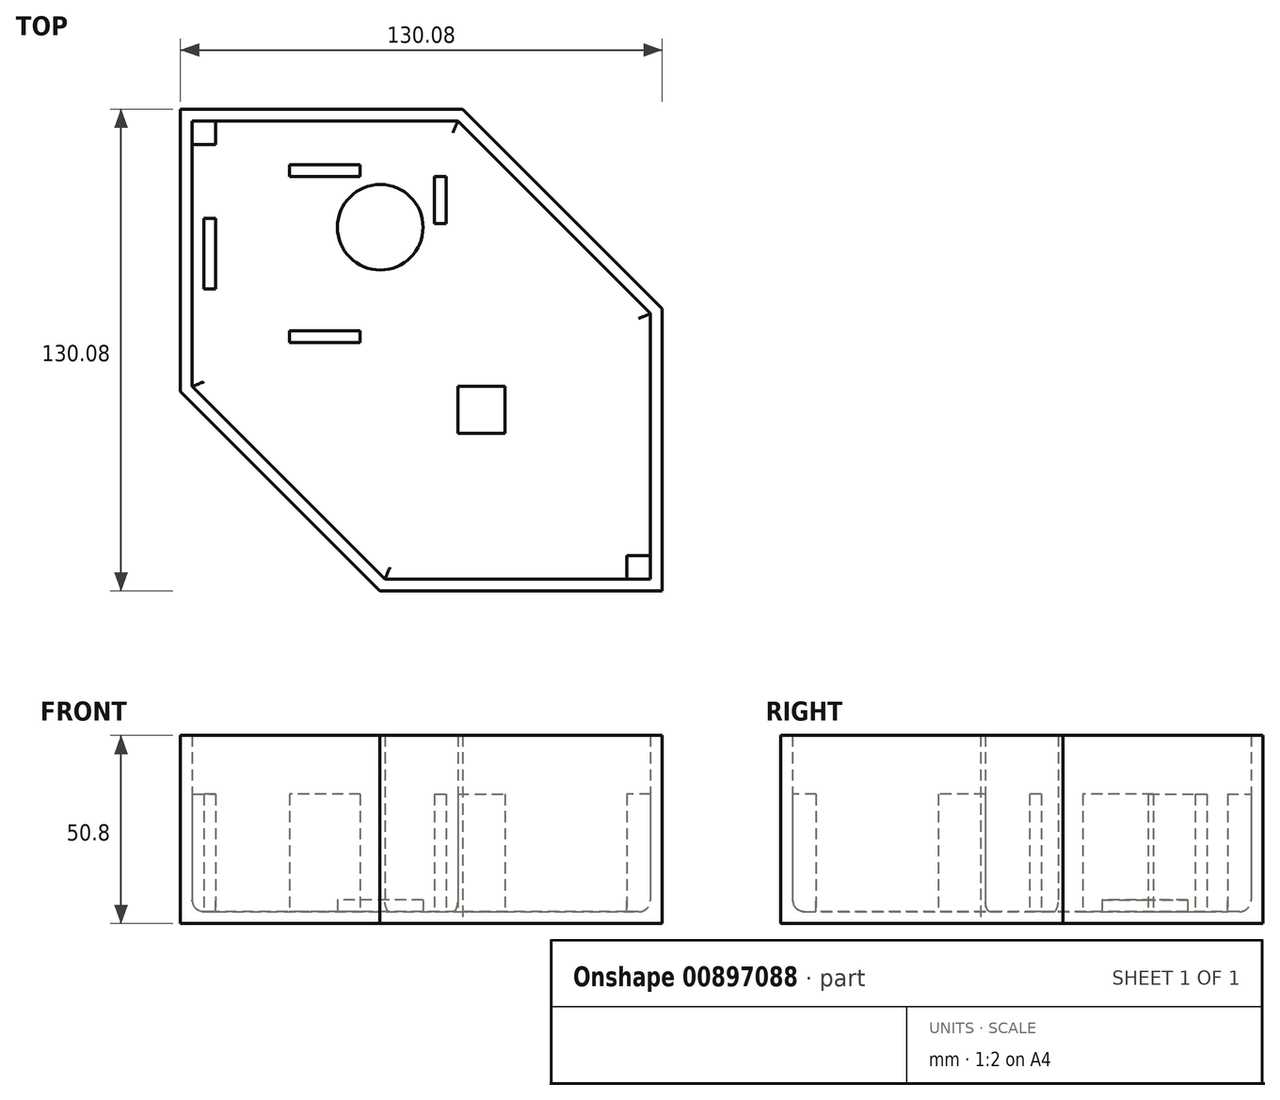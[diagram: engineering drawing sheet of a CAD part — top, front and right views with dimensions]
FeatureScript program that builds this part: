
annotation { "Feature Type Name" : "Feature", "Feature Type Description" : "" }
export const myFeature = defineFeature(function(context is Context, id is Id, definition is map)
    precondition{}
    {
        {
            var Q0;
            Q0=qCreatedBy(makeId("Top.planeOp"),FACE);
            var sketch = newSketch(context, id + "F0", { "sketchPlane" : qUnion([Q0])});
            skLineSegment(sketch, "E0", {"start": v(0, 0) * mm, "end": v(-53.88, 53.88) * mm});
            skLineSegment(sketch, "E1", {"start": v(-53.88, 53.88) * mm, "end": v(-53.88, 130.08) * mm});
            skLineSegment(sketch, "E2", {"start": v(-53.88, 130.08) * mm, "end": v(22.32, 130.08) * mm});
            skLineSegment(sketch, "E3", {"start": v(22.32, 130.08) * mm, "end": v(76.2, 76.2) * mm});
            skLineSegment(sketch, "E4", {"start": v(76.2, 76.2) * mm, "end": v(76.2, 0) * mm});
            skLineSegment(sketch, "E5", {"start": v(76.2, 0) * mm, "end": v(0, 0) * mm});
            skSolve(sketch);
        }
        {
            var Q0;
            Q0=makeQuery(id+"F0.imprint","IMPRINT",FACE,{"disambiguationData":[TD([[makeQuery(id+"F0.imprint","IMPRINT",EDGE,{"derivedFrom":sQuery(id+"F0.wireOp",EDGE,"E0")}),-1.0]])]});
            extrude(context, id + "F1", {"entities" : qUnion([Q0]), "depth" : 50.8 * mm, "offsetDistance" : 25.4 * mm});
        }
        {
            var Q0;
            Q0=makeQuery(id+"F1.opExtrude","CAP_FACE",FACE,{"disambiguationData":[OSD([sQuery(id+"F0.wireOp",EDGE,"E0"),sQuery(id+"F0.wireOp",EDGE,"E1"),sQuery(id+"F0.wireOp",EDGE,"E2"),sQuery(id+"F0.wireOp",EDGE,"E3"),sQuery(id+"F0.wireOp",EDGE,"E4"),sQuery(id+"F0.wireOp",EDGE,"E5")])],"isStart":false});
            shell(context, id + "F2", {"entities" : qUnion([Q0]), "thickness" : 3.17 * mm});
        }
        {
            var Q0;
            Q0=makeQuery(id+"F2.opShell","OFFSET_FACE",FACE,{"disambiguationData":[OSD([sQuery(id+"F0.wireOp",EDGE,"E0"),sQuery(id+"F0.wireOp",EDGE,"E1"),sQuery(id+"F0.wireOp",EDGE,"E2"),sQuery(id+"F0.wireOp",EDGE,"E3"),sQuery(id+"F0.wireOp",EDGE,"E4"),sQuery(id+"F0.wireOp",EDGE,"E5")])]});
            var sketch = newSketch(context, id + "F3", { "sketchPlane" : qUnion([Q0])});
            skLineSegment(sketch, "E6", {"start": v(21, 126.9) * mm, "end": v(21, 3.17) * mm, "construction": true});
            skLineSegment(sketch, "E7", {"start": v(-50.7, 55.2) * mm, "end": v(73.03, 55.2) * mm, "construction": true});
            skLineSegment(sketch, "E8", {"start": v(-14.85, 126.9) * mm, "end": v(-14.85, 55.2) * mm, "construction": true});
            skLineSegment(sketch, "E9", {"start": v(-50.7, 91.05) * mm, "end": v(21, 91.05) * mm, "construction": true});
            skLineSegment(sketch, "E10.bottom", {"start": v(14.69, 111.84) * mm, "end": v(-44.4, 111.84) * mm, "construction": true});
            skLineSegment(sketch, "E10.top", {"start": v(14.69, 70.26) * mm, "end": v(-44.4, 70.26) * mm, "construction": true});
            skLineSegment(sketch, "E10.left", {"start": v(14.69, 111.84) * mm, "end": v(14.69, 70.26) * mm, "construction": true});
            skLineSegment(sketch, "E10.right", {"start": v(-44.4, 111.84) * mm, "end": v(-44.4, 70.26) * mm, "construction": true});
            skPoint(sketch, "E10.middle", {"position": v(-14.85, 91.05) * mm});
            skLineSegment(sketch, "E11.bottom", {"start": v(-5.33, 111.84) * mm, "end": v(-24.38, 111.84) * mm});
            skLineSegment(sketch, "E11.top", {"start": v(-5.33, 115.02) * mm, "end": v(-24.38, 115.02) * mm});
            skLineSegment(sketch, "E11.left", {"start": v(-5.33, 111.84) * mm, "end": v(-5.33, 115.02) * mm});
            skLineSegment(sketch, "E11.right", {"start": v(-24.38, 111.84) * mm, "end": v(-24.38, 115.02) * mm});
            skPoint(sketch, "E11.middle", {"position": v(-14.85, 113.43) * mm});
            skLineSegment(sketch, "E12.bottom", {"start": v(-5.33, 70.26) * mm, "end": v(-24.38, 70.26) * mm});
            skLineSegment(sketch, "E12.top", {"start": v(-5.33, 67.09) * mm, "end": v(-24.38, 67.09) * mm});
            skLineSegment(sketch, "E12.left", {"start": v(-5.33, 70.26) * mm, "end": v(-5.33, 67.09) * mm});
            skLineSegment(sketch, "E12.right", {"start": v(-24.38, 70.26) * mm, "end": v(-24.38, 67.09) * mm});
            skPoint(sketch, "E12.middle", {"position": v(-14.85, 68.67) * mm});
            skLineSegment(sketch, "E13.bottom", {"start": v(-44.4, 100.58) * mm, "end": v(-47.57, 100.58) * mm});
            skLineSegment(sketch, "E13.top", {"start": v(-44.4, 81.53) * mm, "end": v(-47.57, 81.53) * mm});
            skLineSegment(sketch, "E13.left", {"start": v(-44.4, 100.58) * mm, "end": v(-44.4, 81.53) * mm});
            skLineSegment(sketch, "E13.right", {"start": v(-47.57, 100.58) * mm, "end": v(-47.57, 81.53) * mm});
            skPoint(sketch, "E13.middle", {"position": v(-45.98, 91.05) * mm});
            skLineSegment(sketch, "E14.bottom", {"start": v(14.69, 99.14) * mm, "end": v(17.86, 99.14) * mm});
            skLineSegment(sketch, "E14.top", {"start": v(14.69, 111.84) * mm, "end": v(17.86, 111.84) * mm});
            skLineSegment(sketch, "E14.left", {"start": v(14.69, 99.14) * mm, "end": v(14.69, 111.84) * mm});
            skLineSegment(sketch, "E14.right", {"start": v(17.86, 99.14) * mm, "end": v(17.86, 111.84) * mm});
            skLineSegment(sketch, "E15", {"start": v(-24.7, 29.19) * mm, "end": v(47.01, 100.9) * mm, "construction": true});
            skLineSegment(sketch, "E16.bottom", {"start": v(21, 55.2) * mm, "end": v(33.7, 55.2) * mm});
            skLineSegment(sketch, "E16.top", {"start": v(21, 42.5) * mm, "end": v(33.7, 42.5) * mm});
            skLineSegment(sketch, "E16.left", {"start": v(21, 55.2) * mm, "end": v(21, 42.5) * mm});
            skLineSegment(sketch, "E16.right", {"start": v(33.7, 55.2) * mm, "end": v(33.7, 42.5) * mm});
            skLineSegment(sketch, "E17.bottom", {"start": v(73.02, 3.17) * mm, "end": v(66.68, 3.17) * mm});
            skLineSegment(sketch, "E17.top", {"start": v(73.03, 9.53) * mm, "end": v(66.68, 9.53) * mm});
            skLineSegment(sketch, "E17.left", {"start": v(73.02, 3.17) * mm, "end": v(73.02, 9.53) * mm});
            skLineSegment(sketch, "E17.right", {"start": v(66.68, 3.17) * mm, "end": v(66.68, 9.53) * mm});
            skLineSegment(sketch, "E18.bottom", {"start": v(-50.7, 126.9) * mm, "end": v(-44.36, 126.9) * mm});
            skLineSegment(sketch, "E18.top", {"start": v(-50.7, 120.56) * mm, "end": v(-44.36, 120.56) * mm});
            skLineSegment(sketch, "E18.left", {"start": v(-50.7, 126.9) * mm, "end": v(-50.7, 120.56) * mm});
            skLineSegment(sketch, "E18.right", {"start": v(-44.36, 126.9) * mm, "end": v(-44.36, 120.56) * mm});
            skCircle(sketch, "E19", {"center": v(0.06, 98.2) * mm, "radius": 11.56 * mm, "construction": true});
            skSolve(sketch);
        }
        {
            var Q0;
            Q0 = qSketchRegion(id + "F3", true);
            extrude(context, id + "F4", {"entities" : qUnion([Q0]), "operationType" : NewBodyOperationType.ADD, "depth" : 31.75 * mm, "offsetDistance" : 25.4 * mm});
        }
        {
            var Q0;
            Q0=makeQuery(id+"F2.opShell","OFFSET_FACE",FACE,{"disambiguationData":[OSD([sQuery(id+"F0.wireOp",EDGE,"E0"),sQuery(id+"F0.wireOp",EDGE,"E1"),sQuery(id+"F0.wireOp",EDGE,"E2"),sQuery(id+"F0.wireOp",EDGE,"E3"),sQuery(id+"F0.wireOp",EDGE,"E4"),sQuery(id+"F0.wireOp",EDGE,"E5")])]});
            var sketch = newSketch(context, id + "F5", { "sketchPlane" : qUnion([Q0])});
            skCircle(sketch, "E20", {"center": v(0.06, 98.2) * mm, "radius": 11.56 * mm});
            skSolve(sketch);
        }
        {
            var Q0;
            Q0 = qSketchRegion(id + "F5", true);
            extrude(context, id + "F6", {"entities" : qUnion([Q0]), "operationType" : NewBodyOperationType.ADD, "depth" : 3.17 * mm, "offsetDistance" : 25.4 * mm});
        }
        {
            var Q0;
            Q0=makeQuery(id+"F4.opExtrude","CAP_EDGE",EDGE,{"disambiguationData":[OSD([sQuery(id+"F3.wireOp",EDGE,"E14.right")])],"isStart":true});
            var Q1;
            Q1=makeQuery(id+"F4.opExtrude","CAP_EDGE",EDGE,{"disambiguationData":[OSD([sQuery(id+"F3.wireOp",EDGE,"E14.top")])],"isStart":true});
            var Q2;
            Q2=makeQuery(id+"F4.opExtrude","CAP_EDGE",EDGE,{"disambiguationData":[OSD([sQuery(id+"F3.wireOp",EDGE,"E14.bottom")])],"isStart":true});
            var Q3;
            Q3=makeQuery(id+"F4.opExtrude","CAP_EDGE",EDGE,{"disambiguationData":[OSD([sQuery(id+"F3.wireOp",EDGE,"E12.top")])],"isStart":true});
            var Q4;
            Q4=makeQuery(id+"F4.opExtrude","CAP_EDGE",EDGE,{"disambiguationData":[OSD([sQuery(id+"F3.wireOp",EDGE,"E12.left")])],"isStart":true});
            var Q5;
            Q5=makeQuery(id+"F4.opExtrude","CAP_EDGE",EDGE,{"disambiguationData":[OSD([sQuery(id+"F3.wireOp",EDGE,"E12.right")])],"isStart":true});
            var Q6;
            Q6=makeQuery(id+"F4.opExtrude","CAP_EDGE",EDGE,{"disambiguationData":[OSD([sQuery(id+"F3.wireOp",EDGE,"E13.top")])],"isStart":true});
            var Q7;
            Q7=makeQuery(id+"F4.opExtrude","CAP_EDGE",EDGE,{"disambiguationData":[OSD([sQuery(id+"F3.wireOp",EDGE,"E13.right")])],"isStart":true});
            var Q8;
            Q8=makeQuery(id+"F4.opExtrude","CAP_EDGE",EDGE,{"disambiguationData":[OSD([sQuery(id+"F3.wireOp",EDGE,"E13.bottom")])],"isStart":true});
            var Q9;
            Q9=makeQuery(id+"F4.opExtrude","CAP_EDGE",EDGE,{"disambiguationData":[OSD([sQuery(id+"F3.wireOp",EDGE,"E11.right")])],"isStart":true});
            var Q10;
            Q10=makeQuery(id+"F4.opExtrude","CAP_EDGE",EDGE,{"disambiguationData":[OSD([sQuery(id+"F3.wireOp",EDGE,"E11.top")])],"isStart":true});
            var Q11;
            Q11=makeQuery(id+"F4.opExtrude","CAP_EDGE",EDGE,{"disambiguationData":[OSD([sQuery(id+"F3.wireOp",EDGE,"E11.left")])],"isStart":true});
            var Q12;
            Q12=makeQuery(id+"F4.opExtrude","CAP_EDGE",EDGE,{"disambiguationData":[OSD([sQuery(id+"F3.wireOp",EDGE,"E16.bottom")])],"isStart":true});
            var Q13;
            Q13=makeQuery(id+"F4.opExtrude","CAP_EDGE",EDGE,{"disambiguationData":[OSD([sQuery(id+"F3.wireOp",EDGE,"E16.right")])],"isStart":true});
            var Q14;
            Q14=makeQuery(id+"F4.opExtrude","CAP_EDGE",EDGE,{"disambiguationData":[OSD([sQuery(id+"F3.wireOp",EDGE,"E16.top")])],"isStart":true});
            var Q15;
            Q15=makeQuery(id+"F4.opExtrude","CAP_EDGE",EDGE,{"disambiguationData":[OSD([sQuery(id+"F3.wireOp",EDGE,"E16.left")])],"isStart":true});
            var Q16;
            Q16=makeQuery(id+"F4.opExtrude","CAP_EDGE",EDGE,{"disambiguationData":[OSD([sQuery(id+"F3.wireOp",EDGE,"E18.top")])],"isStart":true});
            var Q17;
            Q17=makeQuery(id+"F4.opExtrude","CAP_EDGE",EDGE,{"disambiguationData":[OSD([sQuery(id+"F3.wireOp",EDGE,"E18.right")])],"isStart":true});
            var Q18;
            Q18=makeQuery(id+"F4.opExtrude","CAP_EDGE",EDGE,{"disambiguationData":[OSD([sQuery(id+"F3.wireOp",EDGE,"E17.top")])],"isStart":true});
            var Q19;
            Q19=makeQuery(id+"F4.opExtrude","CAP_EDGE",EDGE,{"disambiguationData":[OSD([sQuery(id+"F3.wireOp",EDGE,"E17.right")])],"isStart":true});
            var Q20;
            {var subQ0=sQuery(id+"F0.wireOp",EDGE,"E2");Q20=makeQuery(id+"F2.opShell","OFFSET_EDGE",EDGE,{"disambiguationData":[OSD([subQ0]),TDD([makeQuery(id+"F1.opExtrude","CAP_EDGE",EDGE,{"disambiguationData":[OSD([subQ0])],"isStart":true})])]});}
            var Q21;
            {var subQ0=sQuery(id+"F0.wireOp",EDGE,"E3");Q21=makeQuery(id+"F2.opShell","OFFSET_EDGE",EDGE,{"disambiguationData":[OSD([subQ0]),TDD([makeQuery(id+"F1.opExtrude","CAP_EDGE",EDGE,{"disambiguationData":[OSD([subQ0])],"isStart":true})])]});}
            var Q22;
            {var subQ0=sQuery(id+"F0.wireOp",EDGE,"E4");Q22=makeQuery(id+"F2.opShell","OFFSET_EDGE",EDGE,{"disambiguationData":[OSD([subQ0]),TDD([makeQuery(id+"F1.opExtrude","CAP_EDGE",EDGE,{"disambiguationData":[OSD([subQ0])],"isStart":true})])]});}
            var Q23;
            {var subQ0=sQuery(id+"F0.wireOp",EDGE,"E5");Q23=makeQuery(id+"F2.opShell","OFFSET_EDGE",EDGE,{"disambiguationData":[OSD([subQ0]),TDD([makeQuery(id+"F1.opExtrude","CAP_EDGE",EDGE,{"disambiguationData":[OSD([subQ0])],"isStart":true})])]});}
            var Q24;
            {var subQ0=sQuery(id+"F0.wireOp",EDGE,"E0");Q24=makeQuery(id+"F2.opShell","OFFSET_EDGE",EDGE,{"disambiguationData":[OSD([subQ0]),TDD([makeQuery(id+"F1.opExtrude","CAP_EDGE",EDGE,{"disambiguationData":[OSD([subQ0])],"isStart":true})])]});}
            var Q25;
            {var subQ0=sQuery(id+"F0.wireOp",EDGE,"E1");Q25=makeQuery(id+"F2.opShell","OFFSET_EDGE",EDGE,{"disambiguationData":[OSD([subQ0]),TDD([makeQuery(id+"F1.opExtrude","CAP_EDGE",EDGE,{"disambiguationData":[OSD([subQ0])],"isStart":true})])]});}
            var Q26;
            Q26=makeQuery(id+"F4.opExtrude","SWEPT_EDGE",EDGE,{"disambiguationData":[OSD([sQuery(id+"F0.wireOp",EDGE,"E1"),sQuery(id+"F3.wireOp",EDGE,"E18.top"),sQuery(id+"F3.wireOp",EDGE,"E18.left")])]});
            var Q27;
            Q27=makeQuery(id+"F4.opExtrude","SWEPT_EDGE",EDGE,{"disambiguationData":[OSD([sQuery(id+"F0.wireOp",EDGE,"E2"),sQuery(id+"F3.wireOp",EDGE,"E18.bottom"),sQuery(id+"F3.wireOp",EDGE,"E18.right")])]});
            var Q28;
            Q28=makeQuery(id+"F4.opExtrude","SWEPT_EDGE",EDGE,{"disambiguationData":[OSD([sQuery(id+"F0.wireOp",EDGE,"E4"),sQuery(id+"F3.wireOp",EDGE,"E17.top"),sQuery(id+"F3.wireOp",EDGE,"E17.left")])]});
            var Q29;
            Q29=makeQuery(id+"F4.opExtrude","SWEPT_EDGE",EDGE,{"disambiguationData":[OSD([sQuery(id+"F0.wireOp",EDGE,"E5"),sQuery(id+"F3.wireOp",EDGE,"E17.bottom"),sQuery(id+"F3.wireOp",EDGE,"E17.right")])]});
            fillet(context, id + "F7", {"entities" : qUnion([Q0, Q1, Q2, Q3, Q4, Q5, Q6, Q7, Q8, Q9, Q10, Q11, Q12, Q13, Q14, Q15, Q16, Q17, Q18, Q19, Q20, Q21, Q22, Q23, Q24, Q25, Q26, Q27, Q28, Q29]), "radius" : 3.17 * mm, "tangentPropagation" : true, "allowEdgeOverflow" : false});
        }
    });
